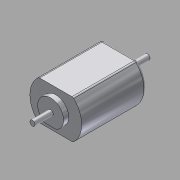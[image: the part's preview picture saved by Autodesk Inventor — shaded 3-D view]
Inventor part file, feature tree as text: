
AUTODESK INVENTOR PART (.ipt)
format: ipt  version: 2015 (Build 190159000, 159)  size: 136,704 bytes
history: native  units: in
note: dims shown in document units (in); Inventor stores cm internally (conversion verified against a paired STEP export)
features: sketch x5, other x3
ambient origin geometry x8: Origin, YZ Plane, XZ Plane, XY Plane, X Axis, Y Axis, Z Axis, Center Point
bodies: Solid1 (feature_tree)
feature tree (8):
  other  "motor.ipt"
  other  "Solid1::motor.ipt"
  other  "TaggingFeature1"
  sketch  "Sketch1"  dims[d0=0.3937in]
  sketch  "Sketch2"
  sketch  "Sketch3"
  sketch  "Sketch4"
  sketch  "Sketch5"
